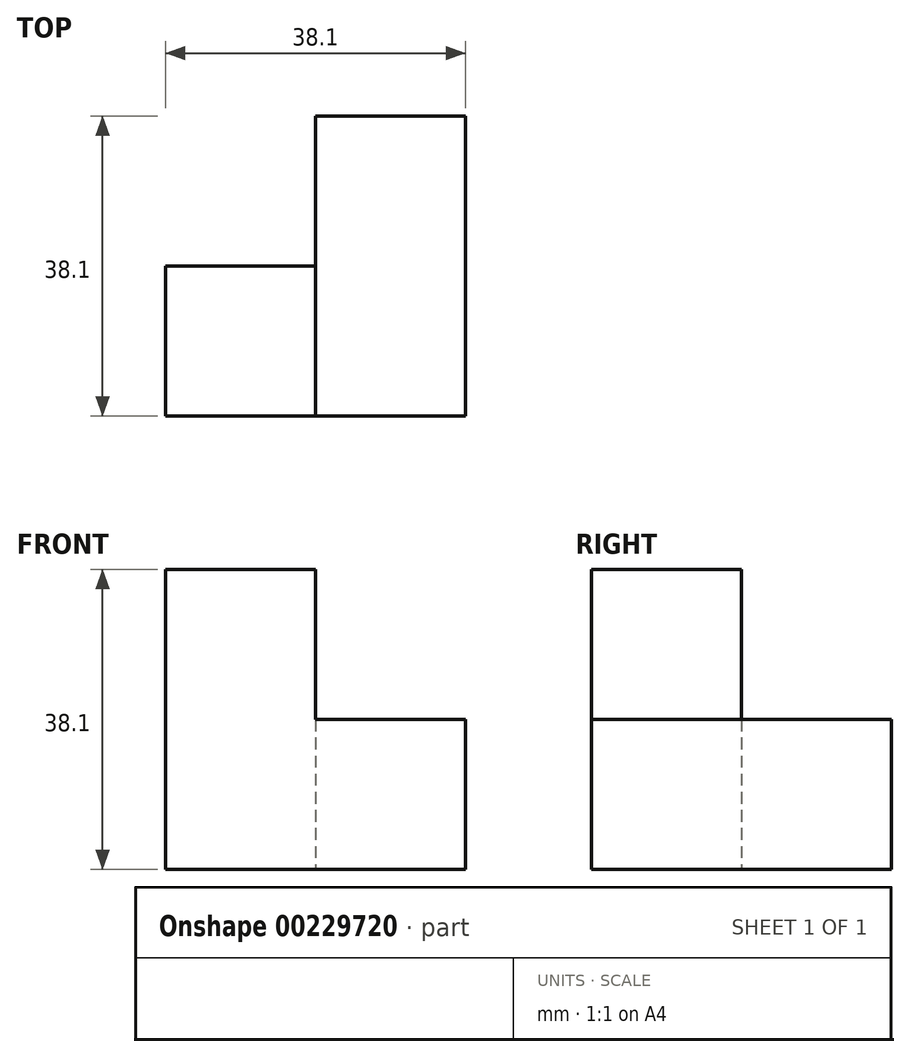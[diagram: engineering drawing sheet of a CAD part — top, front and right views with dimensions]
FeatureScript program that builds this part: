
annotation { "Feature Type Name" : "Feature", "Feature Type Description" : "" }
export const myFeature = defineFeature(function(context is Context, id is Id, definition is map)
    precondition{}
    {
        {
            var Q0;
            Q0=qCreatedBy(makeId("Front.planeOp"),FACE);
            var sketch = newSketch(context, id + "F0", { "sketchPlane" : qUnion([Q0])});
            skLineSegment(sketch, "E0.bottom", {"start": v(-13.41, 9.45) * mm, "end": v(24.69, 9.45) * mm});
            skLineSegment(sketch, "E0.top", {"start": v(-13.41, -9.6) * mm, "end": v(24.69, -9.6) * mm});
            skLineSegment(sketch, "E0.left", {"start": v(-13.41, 9.45) * mm, "end": v(-13.41, -9.6) * mm});
            skLineSegment(sketch, "E0.right", {"start": v(24.69, 9.45) * mm, "end": v(24.69, -9.6) * mm});
            skSolve(sketch);
        }
        {
            var Q0;
            Q0=makeQuery(id+"F0.imprint","IMPRINT",FACE,{"disambiguationData":[TD([[makeQuery(id+"F0.imprint","IMPRINT",EDGE,{"derivedFrom":sQuery(id+"F0.wireOp",EDGE,"E0.bottom")}),-1.0]])]});
            extrude(context, id + "F1", {"entities" : qUnion([Q0]), "depth" : 19.05 * mm});
        }
        {
            var Q0;
            Q0=makeQuery(id+"F1.opExtrude","SWEPT_FACE",FACE,{"disambiguationData":[OSD([sQuery(id+"F0.wireOp",EDGE,"E0.top")])]});
            var sketch = newSketch(context, id + "F2", { "sketchPlane" : qUnion([Q0])});
            skLineSegment(sketch, "E1.bottom", {"start": v(24.69, 0) * mm, "end": v(5.64, 0) * mm});
            skLineSegment(sketch, "E1.top", {"start": v(24.69, -19.05) * mm, "end": v(5.64, -19.05) * mm});
            skLineSegment(sketch, "E1.left", {"start": v(24.69, 0) * mm, "end": v(24.69, -19.05) * mm});
            skLineSegment(sketch, "E1.right", {"start": v(5.64, 0) * mm, "end": v(5.64, -19.05) * mm});
            skSolve(sketch);
        }
        {
            var Q0;
            Q0=makeQuery(id+"F2.imprint","IMPRINT",FACE,{"disambiguationData":[TD([[makeQuery(id+"F2.imprint","IMPRINT",EDGE,{"derivedFrom":sQuery(id+"F2.wireOp",EDGE,"E1.bottom")}),-1.0]])]});
            extrude(context, id + "F3", {"entities" : qUnion([Q0]), "operationType" : NewBodyOperationType.ADD, "oppositeDirection" : true, "depth" : 19.05 * mm});
        }
        {
            var Q0;
            Q0=makeQuery(id+"F3.boolean.opBoolean","MERGE",FACE,{"derivedFrom":[makeQuery(id+"F1.opExtrude","SWEPT_FACE",FACE,{"disambiguationData":[OSD([sQuery(id+"F0.wireOp",EDGE,"E0.bottom")])]}),makeQuery(id+"F3.opExtrude","CAP_FACE",FACE,{"disambiguationData":[OSD([sQuery(id+"F2.wireOp",EDGE,"E1.bottom"),sQuery(id+"F2.wireOp",EDGE,"E1.top"),sQuery(id+"F2.wireOp",EDGE,"E1.left"),sQuery(id+"F2.wireOp",EDGE,"E1.right")])],"isStart":false})]});
            var sketch = newSketch(context, id + "F4", { "sketchPlane" : qUnion([Q0])});
            skLineSegment(sketch, "E2.bottom", {"start": v(5.64, 0) * mm, "end": v(-13.41, 0) * mm});
            skLineSegment(sketch, "E2.top", {"start": v(5.64, -19.05) * mm, "end": v(-13.41, -19.05) * mm});
            skLineSegment(sketch, "E2.left", {"start": v(5.64, 0) * mm, "end": v(5.64, -19.05) * mm});
            skLineSegment(sketch, "E2.right", {"start": v(-13.41, 0) * mm, "end": v(-13.41, -19.05) * mm});
            skSolve(sketch);
        }
        {
            var Q0;
            Q0=makeQuery(id+"F4.imprint","IMPRINT",FACE,{"disambiguationData":[TD([[makeQuery(id+"F4.imprint","IMPRINT",EDGE,{"derivedFrom":sQuery(id+"F4.wireOp",EDGE,"E2.bottom")}),-1.0]])]});
            extrude(context, id + "F5", {"entities" : qUnion([Q0]), "operationType" : NewBodyOperationType.ADD, "depth" : 19.05 * mm});
        }
    });
